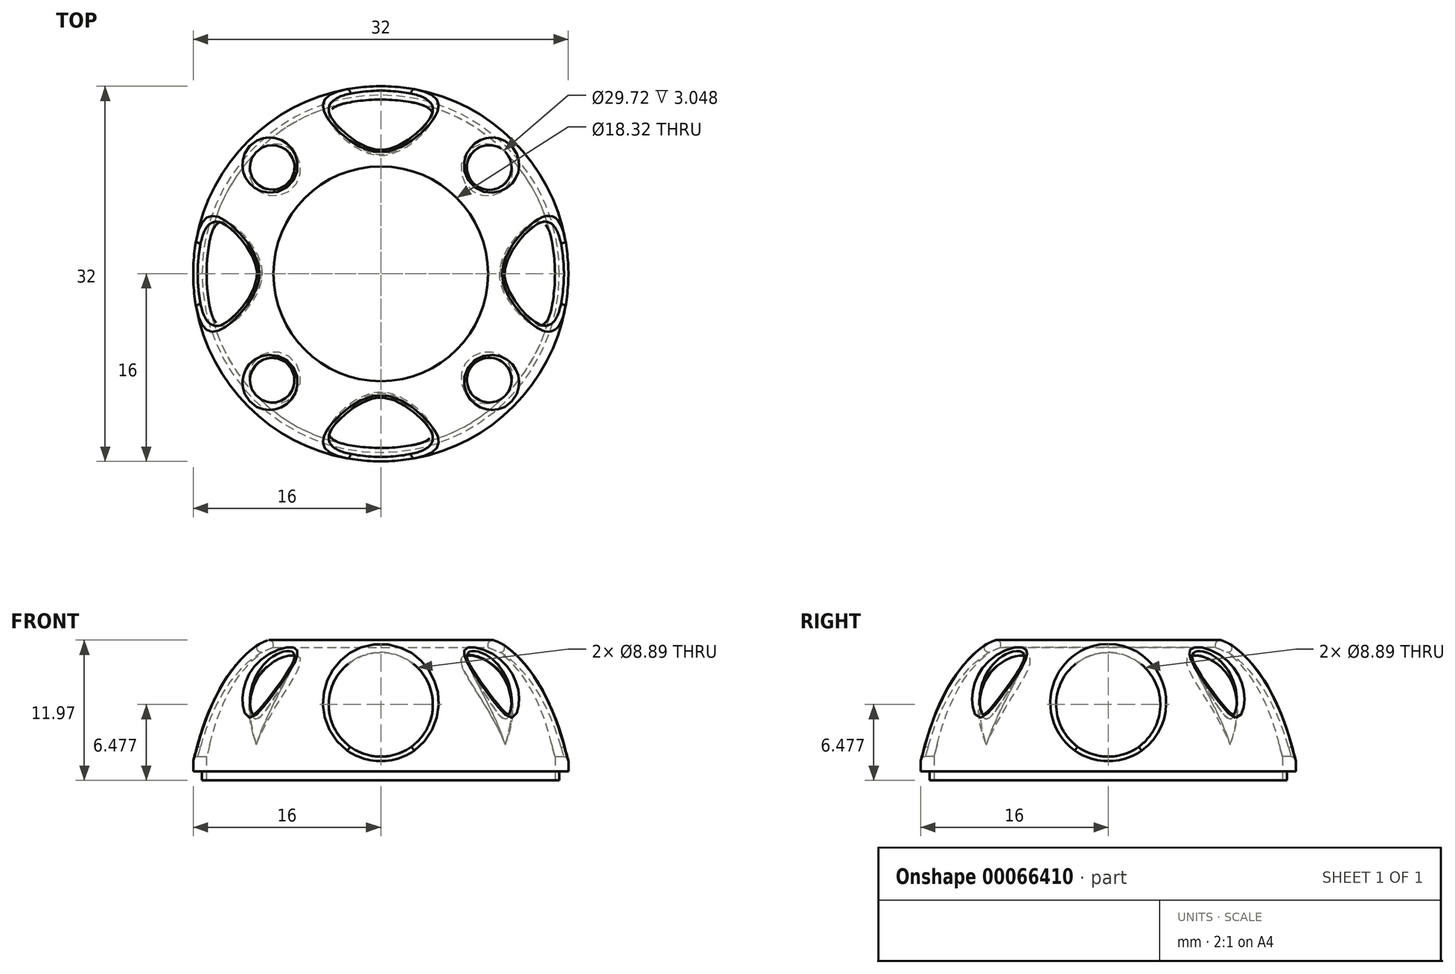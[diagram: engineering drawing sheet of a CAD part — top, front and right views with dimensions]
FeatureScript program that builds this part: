
annotation { "Feature Type Name" : "Feature", "Feature Type Description" : "" }
export const myFeature = defineFeature(function(context is Context, id is Id, definition is map)
    precondition{}
    {
        {
            var Q0;
            Q0=qCreatedBy(makeId("Top.planeOp"),FACE);
            var sketch = newSketch(context, id + "F0", { "sketchPlane" : qUnion([Q0])});
            skCircle(sketch, "E0", {"center": v(0, 0) * mm, "radius": 16 * mm});
            skSolve(sketch);
        }
        {
            var Q0;
            Q0 = qSketchRegion(id + "F0", true);
            extrude(context, id + "F1", {"entities" : qUnion([Q0]), "depth" : 12.7 * mm});
        }
        {
            var Q0;
            Q0=makeQuery(id+"F1.opExtrude","CAP_FACE",FACE,{"disambiguationData":[OSD([sQuery(id+"F0.wireOp",EDGE,"E0")])],"isStart":true});
            var sketch = newSketch(context, id + "F2", { "sketchPlane" : qUnion([Q0])});
            skCircle(sketch, "E1", {"center": v(0, 0) * mm, "radius": 14.86 * mm});
            skSolve(sketch);
        }
        {
            var Q0;
            Q0 = qSketchRegion(id + "F2", true);
            extrude(context, id + "F3", {"entities" : qUnion([Q0]), "operationType" : NewBodyOperationType.REMOVE, "oppositeDirection" : true, "depth" : 11.94 * mm});
        }
        {
            var Q0;
            Q0=makeQuery(id+"F3.boolean.opBoolean","COPY",EDGE,{"derivedFrom":makeQuery(id+"F3.opExtrude","CAP_EDGE",EDGE,{"disambiguationData":[OSD([sQuery(id+"F2.wireOp",EDGE,"E1")])],"isStart":false})});
            fillet(context, id + "F4", {"entities" : qUnion([Q0]), "radius" : 8.9 * mm, "tangentPropagation" : true, "allowEdgeOverflow" : false});
        }
        {
            var Q0;
            Q0=makeQuery(id+"F1.opExtrude","CAP_EDGE",EDGE,{"disambiguationData":[OSD([sQuery(id+"F0.wireOp",EDGE,"E0")])],"isStart":false});
            fillet(context, id + "F5", {"entities" : qUnion([Q0]), "radius" : 10.16 * mm, "tangentPropagation" : true, "allowEdgeOverflow" : false});
        }
        {
            var Q0;
            Q0=makeQuery(id+"F1.opExtrude","CAP_FACE",FACE,{"disambiguationData":[OSD([sQuery(id+"F0.wireOp",EDGE,"E0")])],"isStart":true});
            var sketch = newSketch(context, id + "F6", { "sketchPlane" : qUnion([Q0])});
            skCircle(sketch, "E2", {"center": v(0, 0) * mm, "radius": 15.24 * mm});
            skSolve(sketch);
        }
        {
            var Q0;
            Q0=makeQuery(id+"F6.imprint","IMPRINT",FACE,{"disambiguationData":[TD([[makeQuery(id+"F6.imprint","IMPRINT",EDGE,{"derivedFrom":sQuery(id+"F6.wireOp",EDGE,"E2")}),-1.0]])]});
            extrude(context, id + "F7", {"entities" : qUnion([Q0]), "operationType" : NewBodyOperationType.REMOVE, "oppositeDirection" : true, "depth" : 0.76 * mm});
        }
        {
            var Q0;
            Q0=makeQuery(id+"F1.opExtrude","CAP_FACE",FACE,{"disambiguationData":[OSD([sQuery(id+"F0.wireOp",EDGE,"E0")])],"isStart":false});
            var sketch = newSketch(context, id + "F8", { "sketchPlane" : qUnion([Q0])});
            skCircle(sketch, "E3", {"center": v(0, 0) * mm, "radius": 9.16 * mm});
            skSolve(sketch);
        }
        {
            var Q0;
            Q0 = qSketchRegion(id + "F8", true);
            extrude(context, id + "F9", {"entities" : qUnion([Q0]), "operationType" : NewBodyOperationType.REMOVE, "oppositeDirection" : true, "depth" : 25.4 * mm});
        }
        {
            var Q0;
            Q0=qCreatedBy(makeId("Right.planeOp"),FACE);
            var sketch = newSketch(context, id + "F10", { "sketchPlane" : qUnion([Q0])});
            skCircle(sketch, "E4", {"center": v(0, 6.48) * mm, "radius": 4.45 * mm});
            skSolve(sketch);
        }
        {
            var Q0;
            Q0 = qSketchRegion(id + "F10", true);
            extrude(context, id + "F11", {"entities" : qUnion([Q0]), "operationType" : NewBodyOperationType.REMOVE, "endBound" : BoundingType.SYMMETRIC, "oppositeDirection" : true, "depth" : 33.78 * mm});
        }
        {
            var Q0;
            Q0=qCreatedBy(makeId("Front.planeOp"),FACE);
            var sketch = newSketch(context, id + "F12", { "sketchPlane" : qUnion([Q0])});
            skCircle(sketch, "E5", {"center": v(0, 6.48) * mm, "radius": 4.45 * mm});
            skSolve(sketch);
        }
        {
            var Q0;
            Q0 = qSketchRegion(id + "F12", true);
            extrude(context, id + "F13", {"entities" : qUnion([Q0]), "operationType" : NewBodyOperationType.REMOVE, "endBound" : BoundingType.SYMMETRIC, "oppositeDirection" : true, "depth" : 33.78 * mm});
        }
        {
            var Q0;
            Q0=makeQuery(id+"F9.boolean.opBoolean","INTERSECT",EDGE,{"derivedFrom":[makeQuery(id+"F5.opFillet","BLEND_FACE",FACE,{"disambiguationData":[OSD([sQuery(id+"F0.wireOp",EDGE,"E0")])]}),makeQuery(id+"F9.opExtrude","SWEPT_FACE",FACE,{"disambiguationData":[OSD([sQuery(id+"F8.wireOp",EDGE,"E3")])]})]});
            var Q1;
            Q1=makeQuery(id+"F11.boolean.opBoolean","INTERSECT",EDGE,{"disambiguationData":[OD(0.0)],"derivedFrom":[makeQuery(id+"F5.opFillet","BLEND_FACE",FACE,{"disambiguationData":[OSD([sQuery(id+"F0.wireOp",EDGE,"E0")])]}),makeQuery(id+"F11.opExtrude","SWEPT_FACE",FACE,{"disambiguationData":[OSD([sQuery(id+"F10.wireOp",EDGE,"E4")])]})]});
            var Q2;
            Q2=makeQuery(id+"F13.boolean.opBoolean","INTERSECT",EDGE,{"disambiguationData":[OD(0.0)],"derivedFrom":[makeQuery(id+"F5.opFillet","BLEND_FACE",FACE,{"disambiguationData":[OSD([sQuery(id+"F0.wireOp",EDGE,"E0")])]}),makeQuery(id+"F13.opExtrude","SWEPT_FACE",FACE,{"disambiguationData":[OSD([sQuery(id+"F12.wireOp",EDGE,"E5")])]})]});
            var Q3;
            Q3=makeQuery(id+"F11.boolean.opBoolean","INTERSECT",EDGE,{"disambiguationData":[OD(1.0)],"derivedFrom":[makeQuery(id+"F5.opFillet","BLEND_FACE",FACE,{"disambiguationData":[OSD([sQuery(id+"F0.wireOp",EDGE,"E0")])]}),makeQuery(id+"F11.opExtrude","SWEPT_FACE",FACE,{"disambiguationData":[OSD([sQuery(id+"F10.wireOp",EDGE,"E4")])]})]});
            var Q4;
            Q4=makeQuery(id+"F13.boolean.opBoolean","INTERSECT",EDGE,{"disambiguationData":[OD(1.0)],"derivedFrom":[makeQuery(id+"F5.opFillet","BLEND_FACE",FACE,{"disambiguationData":[OSD([sQuery(id+"F0.wireOp",EDGE,"E0")])]}),makeQuery(id+"F13.opExtrude","SWEPT_FACE",FACE,{"disambiguationData":[OSD([sQuery(id+"F12.wireOp",EDGE,"E5")])]})]});
            fillet(context, id + "F14", {"entities" : qUnion([Q0, Q1, Q2, Q3, Q4]), "radius" : 0.38 * mm, "tangentPropagation" : true, "allowEdgeOverflow" : false});
        }
        {
            var Q0;
            Q0=qCreatedBy(makeId("Top.planeOp"),FACE);
            var sketch = newSketch(context, id + "F15", { "sketchPlane" : qUnion([Q0])});
            skCircle(sketch, "E6", {"center": v(0, 0) * mm, "radius": 12.95 * mm});
            skCircle(sketch, "E7", {"center": v(-9.25, -9.07) * mm, "radius": 1.9 * mm});
            skCircle(sketch, "E8", {"center": v(9.25, -9.07) * mm, "radius": 1.9 * mm});
            skCircle(sketch, "E9", {"center": v(9.25, 9.07) * mm, "radius": 1.9 * mm});
            skCircle(sketch, "E10", {"center": v(-9.25, 9.07) * mm, "radius": 1.9 * mm});
            skSolve(sketch);
        }
        {
            var Q0;
            {var subQ0=sQuery(id+"F15.wireOp",EDGE,"E9");var subQ1=sQuery(id+"F15.wireOp",EDGE,"E6");var subQ2=makeQuery(id+"F15.imprint","INTERSECT",VERTEX,{"disambiguationData":[OD(0.0)],"derivedFrom":[subQ1,subQ0]});Q0=makeQuery(id+"F15.imprint","IMPRINT",FACE,{"disambiguationData":[TD([[makeQuery(id+"F15.imprint","IMPRINT",EDGE,{"disambiguationData":[TD([[subQ2,1.0]])],"derivedFrom":subQ1}),-1.0]])]});}
            var Q1;
            {var subQ0=sQuery(id+"F15.wireOp",EDGE,"E10");var subQ1=sQuery(id+"F15.wireOp",EDGE,"E6");var subQ2=makeQuery(id+"F15.imprint","INTERSECT",VERTEX,{"disambiguationData":[OD(0.0)],"derivedFrom":[subQ1,subQ0]});Q1=makeQuery(id+"F15.imprint","IMPRINT",FACE,{"disambiguationData":[TD([[makeQuery(id+"F15.imprint","IMPRINT",EDGE,{"disambiguationData":[TD([[subQ2,-1.0]])],"derivedFrom":subQ1}),-1.0]])]});}
            var Q2;
            {var subQ0=sQuery(id+"F15.wireOp",EDGE,"E7");var subQ1=sQuery(id+"F15.wireOp",EDGE,"E6");var subQ2=makeQuery(id+"F15.imprint","INTERSECT",VERTEX,{"disambiguationData":[OD(0.0)],"derivedFrom":[subQ1,subQ0]});Q2=makeQuery(id+"F15.imprint","IMPRINT",FACE,{"disambiguationData":[TD([[makeQuery(id+"F15.imprint","IMPRINT",EDGE,{"disambiguationData":[TD([[subQ2,-1.0]])],"derivedFrom":subQ1}),-1.0]])]});}
            var Q3;
            {var subQ0=sQuery(id+"F15.wireOp",EDGE,"E8");var subQ1=sQuery(id+"F15.wireOp",EDGE,"E6");var subQ2=makeQuery(id+"F15.imprint","INTERSECT",VERTEX,{"disambiguationData":[OD(0.0)],"derivedFrom":[subQ1,subQ0]});Q3=makeQuery(id+"F15.imprint","IMPRINT",FACE,{"disambiguationData":[TD([[makeQuery(id+"F15.imprint","IMPRINT",EDGE,{"disambiguationData":[TD([[subQ2,-1.0]])],"derivedFrom":subQ1}),-1.0]])]});}
            var Q4;
            {var subQ0=sQuery(id+"F15.wireOp",EDGE,"E9");var subQ1=sQuery(id+"F15.wireOp",EDGE,"E6");var subQ2=makeQuery(id+"F15.imprint","INTERSECT",VERTEX,{"disambiguationData":[OD(0.0)],"derivedFrom":[subQ1,subQ0]});Q4=makeQuery(id+"F15.imprint","IMPRINT",FACE,{"disambiguationData":[TD([[makeQuery(id+"F15.imprint","IMPRINT",EDGE,{"disambiguationData":[TD([[subQ2,1.0]])],"derivedFrom":subQ1}),1.0]])]});}
            var Q5;
            {var subQ0=sQuery(id+"F15.wireOp",EDGE,"E10");var subQ1=sQuery(id+"F15.wireOp",EDGE,"E6");var subQ2=makeQuery(id+"F15.imprint","INTERSECT",VERTEX,{"disambiguationData":[OD(0.0)],"derivedFrom":[subQ1,subQ0]});Q5=makeQuery(id+"F15.imprint","IMPRINT",FACE,{"disambiguationData":[TD([[makeQuery(id+"F15.imprint","IMPRINT",EDGE,{"disambiguationData":[TD([[subQ2,-1.0]])],"derivedFrom":subQ1}),1.0]])]});}
            var Q6;
            {var subQ0=sQuery(id+"F15.wireOp",EDGE,"E7");var subQ1=sQuery(id+"F15.wireOp",EDGE,"E6");var subQ2=makeQuery(id+"F15.imprint","INTERSECT",VERTEX,{"disambiguationData":[OD(0.0)],"derivedFrom":[subQ1,subQ0]});Q6=makeQuery(id+"F15.imprint","IMPRINT",FACE,{"disambiguationData":[TD([[makeQuery(id+"F15.imprint","IMPRINT",EDGE,{"disambiguationData":[TD([[subQ2,-1.0]])],"derivedFrom":subQ1}),1.0]])]});}
            var Q7;
            {var subQ0=sQuery(id+"F15.wireOp",EDGE,"E8");var subQ1=sQuery(id+"F15.wireOp",EDGE,"E6");var subQ2=makeQuery(id+"F15.imprint","INTERSECT",VERTEX,{"disambiguationData":[OD(0.0)],"derivedFrom":[subQ1,subQ0]});Q7=makeQuery(id+"F15.imprint","IMPRINT",FACE,{"disambiguationData":[TD([[makeQuery(id+"F15.imprint","IMPRINT",EDGE,{"disambiguationData":[TD([[subQ2,-1.0]])],"derivedFrom":subQ1}),1.0]])]});}
            extrude(context, id + "F16", {"entities" : qUnion([Q0, Q1, Q2, Q3, Q4, Q5, Q6, Q7]), "operationType" : NewBodyOperationType.REMOVE, "depth" : 25.4 * mm});
        }
        {
            var Q0;
            Q0=makeQuery(id+"F16.boolean.opBoolean","INTERSECT",EDGE,{"derivedFrom":[makeQuery(id+"F4.opFillet","BLEND_FACE",FACE,{"disambiguationData":[OSD([sQuery(id+"F2.wireOp",EDGE,"E1")])]}),makeQuery(id+"F16.opExtrude","SWEPT_FACE",FACE,{"disambiguationData":[OSD([sQuery(id+"F15.wireOp",EDGE,"E7")])]})]});
            var Q1;
            Q1=makeQuery(id+"F16.boolean.opBoolean","INTERSECT",EDGE,{"derivedFrom":[makeQuery(id+"F4.opFillet","BLEND_FACE",FACE,{"disambiguationData":[OSD([sQuery(id+"F2.wireOp",EDGE,"E1")])]}),makeQuery(id+"F16.opExtrude","SWEPT_FACE",FACE,{"disambiguationData":[OSD([sQuery(id+"F15.wireOp",EDGE,"E8")])]})]});
            var Q2;
            Q2=makeQuery(id+"F16.boolean.opBoolean","INTERSECT",EDGE,{"derivedFrom":[makeQuery(id+"F4.opFillet","BLEND_FACE",FACE,{"disambiguationData":[OSD([sQuery(id+"F2.wireOp",EDGE,"E1")])]}),makeQuery(id+"F16.opExtrude","SWEPT_FACE",FACE,{"disambiguationData":[OSD([sQuery(id+"F15.wireOp",EDGE,"E10")])]})]});
            var Q3;
            Q3=makeQuery(id+"F16.boolean.opBoolean","INTERSECT",EDGE,{"derivedFrom":[makeQuery(id+"F4.opFillet","BLEND_FACE",FACE,{"disambiguationData":[OSD([sQuery(id+"F2.wireOp",EDGE,"E1")])]}),makeQuery(id+"F16.opExtrude","SWEPT_FACE",FACE,{"disambiguationData":[OSD([sQuery(id+"F15.wireOp",EDGE,"E9")])]})]});
            var Q4;
            Q4=makeQuery(id+"F16.boolean.opBoolean","INTERSECT",EDGE,{"derivedFrom":[makeQuery(id+"F5.opFillet","BLEND_FACE",FACE,{"disambiguationData":[OSD([sQuery(id+"F0.wireOp",EDGE,"E0")])]}),makeQuery(id+"F16.opExtrude","SWEPT_FACE",FACE,{"disambiguationData":[OSD([sQuery(id+"F15.wireOp",EDGE,"E10")])]})]});
            var Q5;
            Q5=makeQuery(id+"F16.boolean.opBoolean","INTERSECT",EDGE,{"derivedFrom":[makeQuery(id+"F5.opFillet","BLEND_FACE",FACE,{"disambiguationData":[OSD([sQuery(id+"F0.wireOp",EDGE,"E0")])]}),makeQuery(id+"F16.opExtrude","SWEPT_FACE",FACE,{"disambiguationData":[OSD([sQuery(id+"F15.wireOp",EDGE,"E7")])]})]});
            var Q6;
            Q6=makeQuery(id+"F16.boolean.opBoolean","INTERSECT",EDGE,{"derivedFrom":[makeQuery(id+"F5.opFillet","BLEND_FACE",FACE,{"disambiguationData":[OSD([sQuery(id+"F0.wireOp",EDGE,"E0")])]}),makeQuery(id+"F16.opExtrude","SWEPT_FACE",FACE,{"disambiguationData":[OSD([sQuery(id+"F15.wireOp",EDGE,"E8")])]})]});
            var Q7;
            Q7=makeQuery(id+"F16.boolean.opBoolean","INTERSECT",EDGE,{"derivedFrom":[makeQuery(id+"F5.opFillet","BLEND_FACE",FACE,{"disambiguationData":[OSD([sQuery(id+"F0.wireOp",EDGE,"E0")])]}),makeQuery(id+"F16.opExtrude","SWEPT_FACE",FACE,{"disambiguationData":[OSD([sQuery(id+"F15.wireOp",EDGE,"E9")])]})]});
            fillet(context, id + "F17", {"entities" : qUnion([Q0, Q1, Q2, Q3, Q4, Q5, Q6, Q7]), "radius" : 0.38 * mm, "tangentPropagation" : true, "allowEdgeOverflow" : false});
        }
    });
